# Revit family: LC-7
name_source: partatom
category: Generic Models
revit_build: Autodesk Revit 2017 (Build: 20170419_0315(x64)
units: mm (PartAtom-declared; Revit-internal decimal feet)

## family parameters
Always vertical = Yes
Can host rebar = No
Cut with Voids When Loaded = No
Host = Wall
Part Type = Normal
Room Calculation Point = No
Round Connector Dimension = Use Diameter
Shared = No

## types (3) — shared parameters
Depth = 88 mm
Height = 870 mm  [stored 2.85433 ft]
Keynote = 6120
Manufacturer = Sentakia Oy
Materiaali = kromattu messinki (CuZn36As)
Sentakia_Material_Default = Stainless Steel, Polished_sentakia
URL = http://www.sentakia.com

## per-type parameters (varying)
| type | EAN | LVI | Leveys | Model | Teho |
| 350 | 4770046007146 | 5489945 | 350 mm | LS-7/350 | kromi: 104 W maalattu: 135 W |
| 500 | 4770046007153 | 5489946 | 500 mm | LS-7/500 | kromi: 120 W maalattu: 156 W |
| 600 | 4770046007160 | 5489947 | 600 mm | LS-7/600 | kromi: 127 W maalattu: 165 W |

note: [stored X ft] marks values corroborated as IEEE doubles in the binary element streams (Revit-internal decimal feet)

## geometry (parser evidence)
native form markers: Blend x4, Sweep x2
no freeform markers — native parametric forms only
